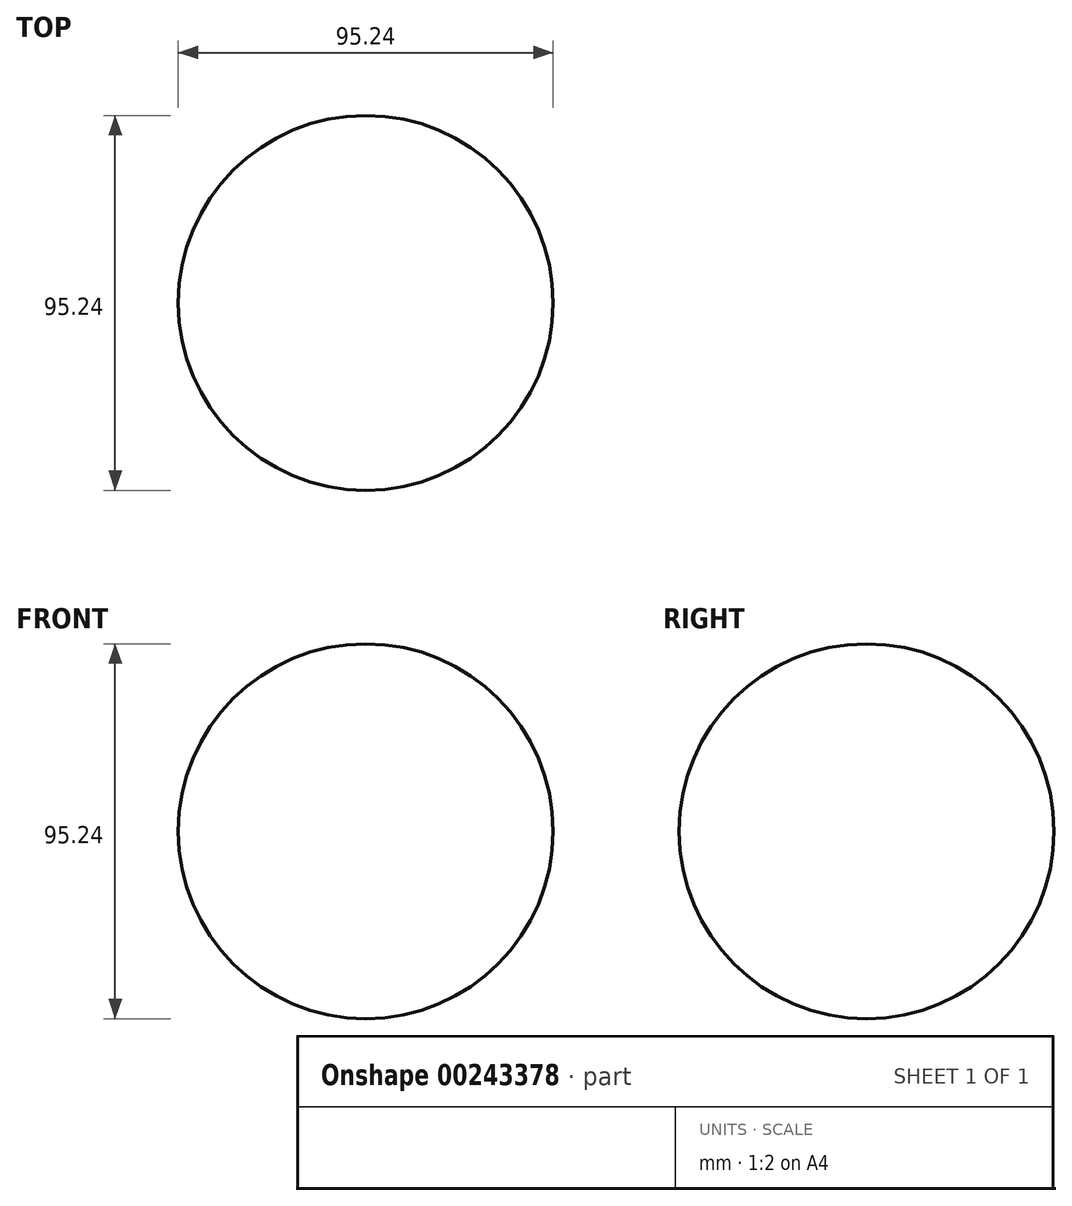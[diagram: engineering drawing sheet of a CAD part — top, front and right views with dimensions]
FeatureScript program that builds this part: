
annotation { "Feature Type Name" : "Feature", "Feature Type Description" : "" }
export const myFeature = defineFeature(function(context is Context, id is Id, definition is map)
    precondition{}
    {
        {
            var Q0;
            Q0=qCreatedBy(makeId("Front.planeOp"),FACE);
            var sketch = newSketch(context, id + "F0", { "sketchPlane" : qUnion([Q0])});
            skArc(sketch, "E0", {"start": v(0, -47.63) * mm, "mid": v(47.63, 0) * mm, "end": v(0, 47.63) * mm});
            skLineSegment(sketch, "E1", {"start": v(0, 47.63) * mm, "end": v(0, -47.63) * mm});
            skSolve(sketch);
        }
        {
            var Q0;
            Q0 = qSketchRegion(id + "F0", true);
            var Q1;
            Q1=sQuery(id+"F0.wireOp",EDGE,"E1");
            revolve(context, id + "F1", {"entities" : qUnion([Q0]), "axis" : qUnion([Q1]), "revolveType" : RevolveType.FULL});
        }
    });
